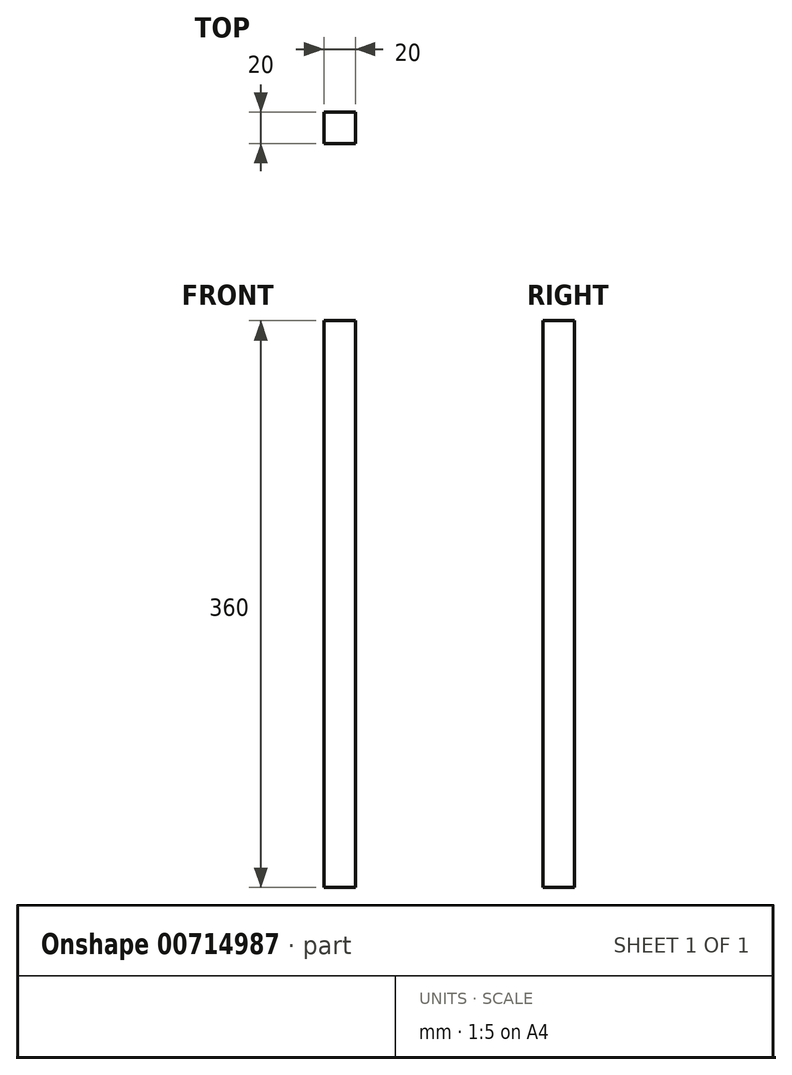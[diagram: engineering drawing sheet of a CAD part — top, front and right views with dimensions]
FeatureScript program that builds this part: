
annotation { "Feature Type Name" : "Feature", "Feature Type Description" : "" }
export const myFeature = defineFeature(function(context is Context, id is Id, definition is map)
    precondition{}
    {
        {
            var Q0;
            Q0=qCreatedBy(makeId("Top.planeOp"),FACE);
            var sketch = newSketch(context, id + "F0", { "sketchPlane" : qUnion([Q0])});
            skLineSegment(sketch, "E0.bottom", {"start": v(10, -10) * mm, "end": v(-10, -10) * mm});
            skLineSegment(sketch, "E0.top", {"start": v(10, 10) * mm, "end": v(-10, 10) * mm});
            skLineSegment(sketch, "E0.left", {"start": v(10, -10) * mm, "end": v(10, 10) * mm});
            skLineSegment(sketch, "E0.right", {"start": v(-10, -10) * mm, "end": v(-10, 10) * mm});
            skPoint(sketch, "E0.middle", {"position": v(0, 0) * mm});
            skSolve(sketch);
        }
        {
            var Q0;
            Q0 = qSketchRegion(id + "F0", true);
            extrude(context, id + "F1", {"entities" : qUnion([Q0]), "depth" : 360 * mm, "offsetDistance" : 25 * mm});
        }
        {
            var Q0;
            Q0 = qSketchRegion(id + "F0", true);
            extrude(context, id + "F2", {"entities" : qUnion([Q0]), "depth" : 360 * mm, "offsetDistance" : 25 * mm});
        }
    });
